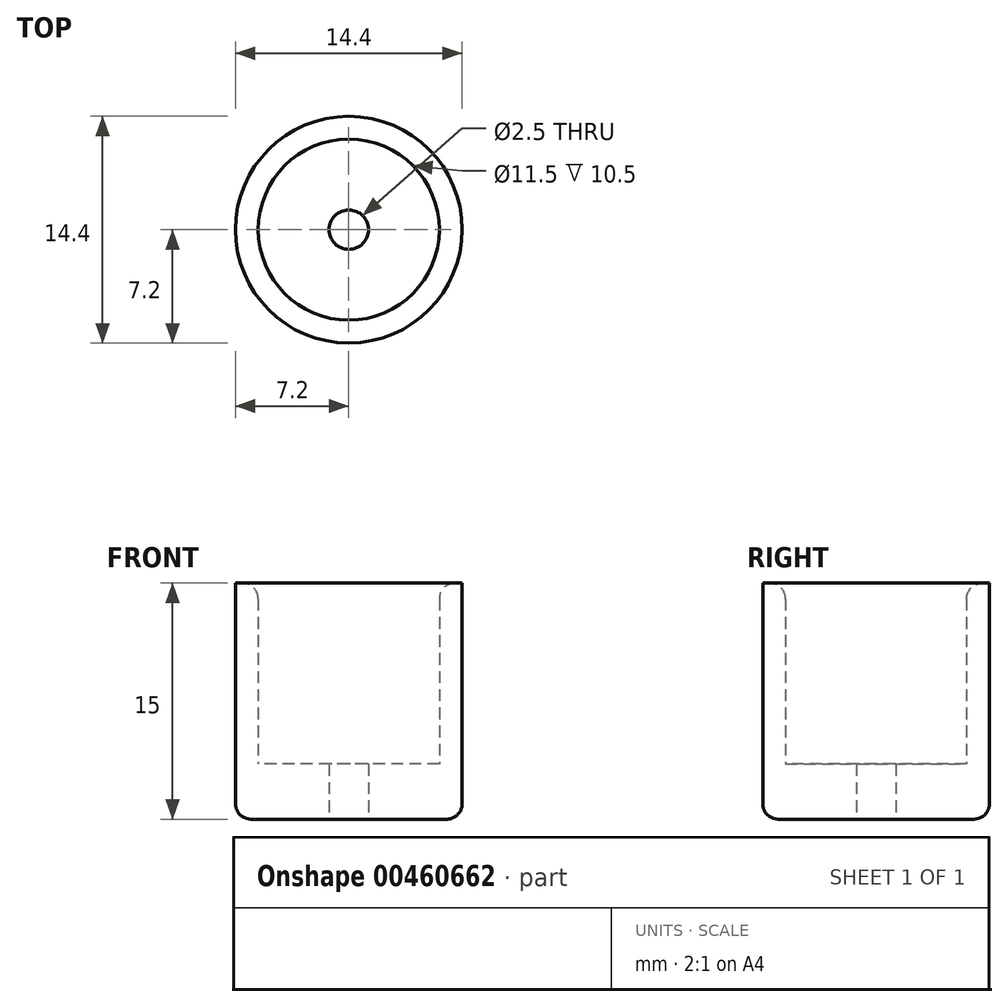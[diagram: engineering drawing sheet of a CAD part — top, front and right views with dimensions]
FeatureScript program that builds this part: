
annotation { "Feature Type Name" : "Feature", "Feature Type Description" : "" }
export const myFeature = defineFeature(function(context is Context, id is Id, definition is map)
    precondition{}
    {
        {
            var Q0;
            Q0=qCreatedBy(makeId("Top.planeOp"),FACE);
            var sketch = newSketch(context, id + "F0", { "sketchPlane" : qUnion([Q0])});
            skCircle(sketch, "E0", {"center": v(0, 0) * mm, "radius": 7.2 * mm});
            skCircle(sketch, "E1", {"center": v(0, 0) * mm, "radius": 1.25 * mm});
            skSolve(sketch);
        }
        {
            var Q0;
            Q0=makeQuery(id+"F0.imprint","IMPRINT",FACE,{"disambiguationData":[TD([[makeQuery(id+"F0.imprint","IMPRINT",EDGE,{"derivedFrom":sQuery(id+"F0.wireOp",EDGE,"E0")}),1.0]])]});
            extrude(context, id + "F1", {"entities" : qUnion([Q0]), "depth" : 3.5 * mm});
        }
        {
            var Q0;
            Q0=qCreatedBy(makeId("Top.planeOp"),FACE);
            var sketch = newSketch(context, id + "F2", { "sketchPlane" : qUnion([Q0])});
            skCircle(sketch, "E2", {"center": v(0, 0) * mm, "radius": 7.2 * mm});
            skCircle(sketch, "E3", {"center": v(0, 0) * mm, "radius": 5.75 * mm});
            skSolve(sketch);
        }
        {
            var Q0;
            Q0 = qSketchRegion(id + "F2", true);
            extrude(context, id + "F3", {"entities" : qUnion([Q0]), "operationType" : NewBodyOperationType.ADD, "depth" : 15 * mm});
        }
        {
            var Q0;
            Q0=makeQuery(id+"F1.opExtrude","CAP_EDGE",EDGE,{"disambiguationData":[OSD([sQuery(id+"F0.wireOp",EDGE,"E0")])],"isStart":true});
            var Q1;
            Q1=makeQuery(id+"F3.opExtrude","CAP_EDGE",EDGE,{"disambiguationData":[OSD([sQuery(id+"F2.wireOp",EDGE,"E3")])],"isStart":false});
            fillet(context, id + "F4", {"entities" : qUnion([Q0, Q1]), "radius" : 1 * mm, "tangentPropagation" : true, "allowEdgeOverflow" : false});
        }
    });
